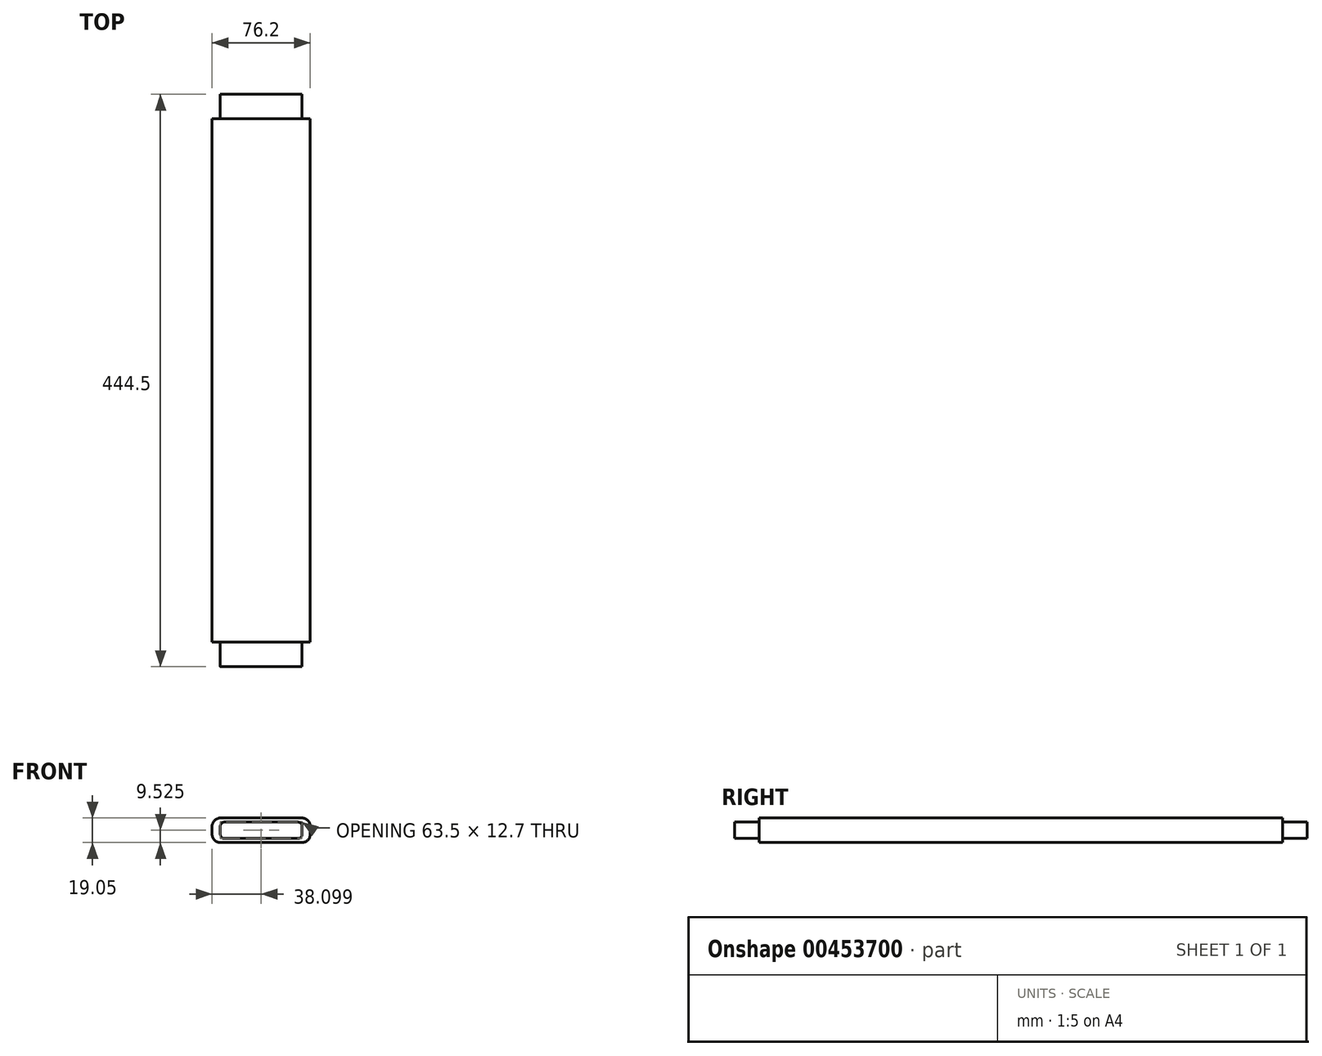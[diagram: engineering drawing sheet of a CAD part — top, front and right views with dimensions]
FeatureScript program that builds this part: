
annotation { "Feature Type Name" : "Feature", "Feature Type Description" : "" }
export const myFeature = defineFeature(function(context is Context, id is Id, definition is map)
    precondition{}
    {
        {
            var Q0;
            Q0=qCreatedBy(makeId("Front.planeOp"),FACE);
            var sketch = newSketch(context, id + "F0", { "sketchPlane" : qUnion([Q0])});
            skLineSegment(sketch, "E0", {"start": v(-34.62, 29.9) * mm, "end": v(41.58, 29.9) * mm});
            skLineSegment(sketch, "E1", {"start": v(41.58, 29.9) * mm, "end": v(41.58, 10.86) * mm});
            skLineSegment(sketch, "E2", {"start": v(41.58, 10.86) * mm, "end": v(-34.62, 10.86) * mm});
            skLineSegment(sketch, "E3", {"start": v(-34.62, 10.86) * mm, "end": v(-34.62, 29.9) * mm});
            skSolve(sketch);
        }
        {
            var Q0;
            Q0 = qSketchRegion(id + "F0", true);
            extrude(context, id + "F1", {"entities" : qUnion([Q0]), "oppositeDirection" : true, "depth" : 406.4 * mm});
        }
        {
            var Q0;
            Q0=makeQuery(id+"F1.opExtrude","CAP_FACE",FACE,{"disambiguationData":[OSD([sQuery(id+"F0.wireOp",EDGE,"E0"),sQuery(id+"F0.wireOp",EDGE,"E1"),sQuery(id+"F0.wireOp",EDGE,"E2"),sQuery(id+"F0.wireOp",EDGE,"E3")])],"isStart":true});
            var sketch = newSketch(context, id + "F2", { "sketchPlane" : qUnion([Q0])});
            skLineSegment(sketch, "E4", {"start": v(-28.27, 26.73) * mm, "end": v(35.23, 26.73) * mm});
            skLineSegment(sketch, "E5", {"start": v(35.23, 26.73) * mm, "end": v(35.23, 14.03) * mm});
            skLineSegment(sketch, "E6", {"start": v(35.23, 14.03) * mm, "end": v(-28.27, 14.03) * mm});
            skLineSegment(sketch, "E7", {"start": v(-28.27, 14.03) * mm, "end": v(-28.27, 26.73) * mm});
            skSolve(sketch);
        }
        {
            var Q0;
            Q0=makeQuery(id+"F2.imprint","IMPRINT",FACE,{"disambiguationData":[TD([[makeQuery(id+"F2.imprint","IMPRINT",EDGE,{"derivedFrom":sQuery(id+"F2.wireOp",EDGE,"E4")}),-1.0]])]});
            extrude(context, id + "F3", {"entities" : qUnion([Q0]), "operationType" : NewBodyOperationType.ADD, "depth" : 19.05 * mm});
        }
        {
            var Q0;
            Q0=makeQuery(id+"F1.opExtrude","SWEPT_EDGE",EDGE,{"disambiguationData":[OSD([sQuery(id+"F0.wireOp",EDGE,"E0"),sQuery(id+"F0.wireOp",EDGE,"E1")])]});
            var Q1;
            Q1=makeQuery(id+"F1.opExtrude","SWEPT_EDGE",EDGE,{"disambiguationData":[OSD([sQuery(id+"F0.wireOp",EDGE,"E1"),sQuery(id+"F0.wireOp",EDGE,"E2")])]});
            var Q2;
            Q2=makeQuery(id+"F1.opExtrude","SWEPT_EDGE",EDGE,{"disambiguationData":[OSD([sQuery(id+"F0.wireOp",EDGE,"E0"),sQuery(id+"F0.wireOp",EDGE,"E3")])]});
            var Q3;
            Q3=makeQuery(id+"F1.opExtrude","SWEPT_EDGE",EDGE,{"disambiguationData":[OSD([sQuery(id+"F0.wireOp",EDGE,"E2"),sQuery(id+"F0.wireOp",EDGE,"E3")])]});
            fillet(context, id + "F4", {"entities" : qUnion([Q0, Q1, Q2, Q3]), "radius" : 6.35 * mm, "tangentPropagation" : true, "allowEdgeOverflow" : false});
        }
        {
            var Q0;
            Q0=makeQuery(id+"F1.opExtrude","CAP_FACE",FACE,{"disambiguationData":[OSD([sQuery(id+"F0.wireOp",EDGE,"E0"),sQuery(id+"F0.wireOp",EDGE,"E1"),sQuery(id+"F0.wireOp",EDGE,"E2"),sQuery(id+"F0.wireOp",EDGE,"E3")])],"isStart":false});
            var sketch = newSketch(context, id + "F5", { "sketchPlane" : qUnion([Q0])});
            skLineSegment(sketch, "E8", {"start": v(-35.23, 26.73) * mm, "end": v(28.27, 26.73) * mm});
            skLineSegment(sketch, "E9", {"start": v(28.27, 26.73) * mm, "end": v(28.27, 14.03) * mm});
            skLineSegment(sketch, "E10", {"start": v(28.27, 14.03) * mm, "end": v(-35.23, 14.03) * mm});
            skLineSegment(sketch, "E11", {"start": v(-35.23, 14.03) * mm, "end": v(-35.23, 26.73) * mm});
            skSolve(sketch);
        }
        {
            var Q0;
            Q0 = qSketchRegion(id + "F5", true);
            extrude(context, id + "F6", {"entities" : qUnion([Q0]), "operationType" : NewBodyOperationType.ADD, "depth" : 19.05 * mm});
        }
        {
            var Q0;
            Q0=makeQuery(id+"F3.opExtrude","SWEPT_EDGE",EDGE,{"disambiguationData":[OSD([sQuery(id+"F2.wireOp",EDGE,"E4"),sQuery(id+"F2.wireOp",EDGE,"E5")])]});
            var Q1;
            Q1=makeQuery(id+"F3.opExtrude","SWEPT_EDGE",EDGE,{"disambiguationData":[OSD([sQuery(id+"F2.wireOp",EDGE,"E5"),sQuery(id+"F2.wireOp",EDGE,"E6")])]});
            var Q2;
            Q2=makeQuery(id+"F3.opExtrude","SWEPT_EDGE",EDGE,{"disambiguationData":[OSD([sQuery(id+"F2.wireOp",EDGE,"E4"),sQuery(id+"F2.wireOp",EDGE,"E7")])]});
            var Q3;
            Q3=makeQuery(id+"F3.opExtrude","SWEPT_EDGE",EDGE,{"disambiguationData":[OSD([sQuery(id+"F2.wireOp",EDGE,"E6"),sQuery(id+"F2.wireOp",EDGE,"E7")])]});
            fillet(context, id + "F7", {"entities" : qUnion([Q0, Q1, Q2, Q3]), "radius" : 3.17 * mm, "tangentPropagation" : true, "allowEdgeOverflow" : false});
        }
    });
